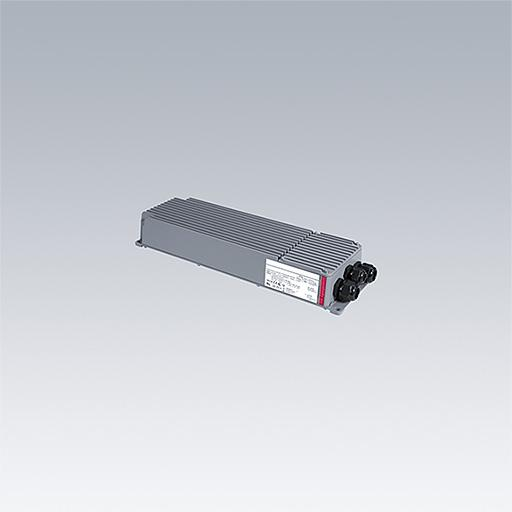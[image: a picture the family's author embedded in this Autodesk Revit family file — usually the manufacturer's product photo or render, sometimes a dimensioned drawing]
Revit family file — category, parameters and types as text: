
# Revit family: Thorn ALTIS GEN5 Gearbox-2 channel gearbox for BW
name_source: partatom
category: Electrical Fixtures
units: mm (PartAtom-declared; Revit-internal decimal feet)

## family parameters
Cut with Voids When Loaded = Yes
Host = Face
Maintain Annotation Orientation = No
Part Type = Normal
Room Calculation Point = Yes
Round Connector Dimension = Use Diameter
Shared = Yes

## types (4) — shared parameters
Apparent Load = 1400 VA
Assembly Code = Pr_60_70_48_54
Description = LED Control Gear
Export Type to IFC As = IfcLightFixtureType
Lamp = LED
Luminaire Height = 77 mm  [stored 0.252625 ft]
Luminaire Length = 500 mm  [stored 1.64042 ft]
Luminaire Width = 152 mm  [stored 0.498688 ft]
Manufacturer = Thorn Lighting
Material Housing = Thorn-Aluminium-RAL 7043-Traffic Grey B
Power Factor = 1
Type IFC Predefined Type = DIRECTIONSOURCE
Type Image = TLG_ALG5_F_GB_LE_2100W.jpg
URL = https://www.thornlighting.com
Wattage = 1400 W
zero-valued in all types: Default Elevation

## per-type parameters (varying)
| type | Model |
| ALG5 GB LE 1400W 0.85A 550V 2CH BW DA | 96800228 |
| ALG5 GB LE 1400W 0.85A 550V 2CH BW RDMX | 96800231 |
| ALG5 GB LE 1400W 1.05A 550V 2CH BW DA | 96800227 |
| ALG5 GB LE 1400W 1.05A 550V 2CH BW RDMX | 96800230 |

note: [stored X ft] marks values corroborated as IEEE doubles in the binary element streams (Revit-internal decimal feet)

## geometry (parser evidence)
native form markers: Sweep x2
no freeform markers — native parametric forms only
